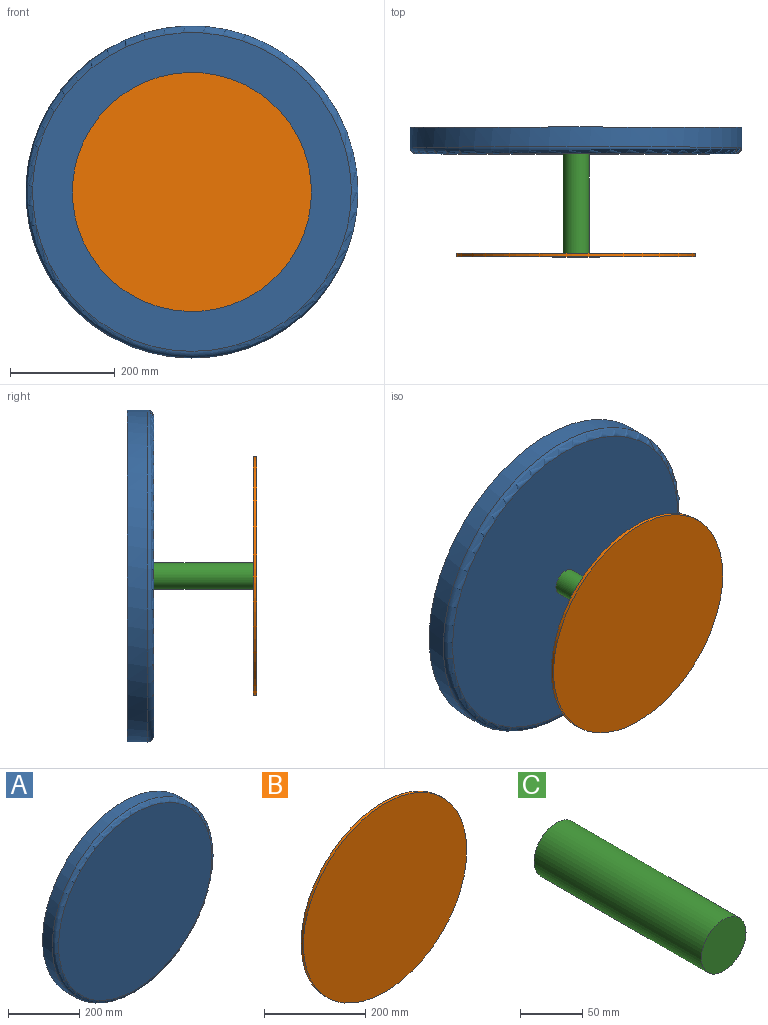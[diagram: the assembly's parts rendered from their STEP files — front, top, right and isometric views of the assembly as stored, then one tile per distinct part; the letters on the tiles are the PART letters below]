
ASSEMBLY  parts=3 mates=2
PART A: 4 faces, bbox 687.3x50.8x687.3 mm
  f0: cylinder r=317.5mm len=635mm, axis (0,1,0), area 76006.1mm2, adj f2,f3
  f1: plane 609.6x609.6mm, normal (0,-1,0), area 291863.5mm2, adj f3
  f2: plane 635x635mm, normal (0,1,0), area 316692.2mm2, adj f0
  f3: torus R=304.8mm, axis (0,-1,0), area 39218.3mm2, adj f0,f1
PART B: 3 faces, bbox 457.2x6.4x457.2 mm
  f0: cylinder r=228.6mm len=457.2mm, axis (0,1,0), area 9120.7mm2, adj f1,f2
  f1: plane 457.2x457.2mm, normal (0,-1,0), area 164173.2mm2, adj f0
  f2: plane 457.2x457.2mm, normal (0,1,0), area 164173.2mm2, adj f0
PART C: 3 faces, bbox 50.8x190.5x50.8 mm
  f0: cylinder r=25.4mm len=190.5mm, axis (0,1,0), area 30402.4mm2, adj f1,f2
  f1: plane 50.8x50.8mm, normal (0,-1,0), area 2026.8mm2, adj f0
  f2: plane 50.8x50.8mm, normal (0,1,0), area 2026.8mm2, adj f0
PLACE A t=(-59.87,266.83,-91.51)mm
PLACE B t=(-59.87,25.53,-91.51)mm
PLACE C t=(-59.87,216.03,-91.51)mm
MATE fastened C.f0 <-> A.f0  axis (0,1,0) through (-59.87,216.03,-91.51)mm
MATE revolute C.f0 <-> B.f0  axis (0,-1,0) through (-59.87,25.53,-91.51)mm
